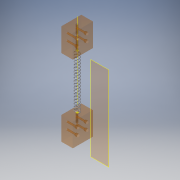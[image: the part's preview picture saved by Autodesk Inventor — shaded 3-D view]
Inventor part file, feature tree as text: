
AUTODESK INVENTOR PART (.ipt)
format: ipt  version: 2016 (Build 200138000, 138)  size: 158,208 bytes
history: native  units: in
note: dims shown in document units (in); Inventor stores cm internally (conversion verified against a paired STEP export)
features: surface_op x2, other x2, plane x1
ambient origin geometry x8: Origin, YZ Plane, XZ Plane, XY Plane, X Axis, Y Axis, Z Axis, Center Point
bodies: Body1 (feature_tree), Body2 (feature_tree)
feature tree (5):
  plane  "Work Plane1"
  surface_op  "Surface1"
  surface_op  "Surface2"
  other  "Srf1"
  other  "Srf2"
